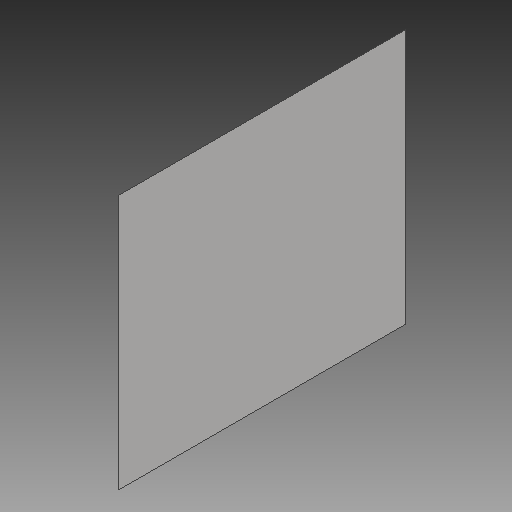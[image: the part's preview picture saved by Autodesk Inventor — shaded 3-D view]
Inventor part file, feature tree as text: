
AUTODESK INVENTOR PART (.ipt)
format: ipt  version: 2018 (Build 220112000, 112)  size: 78,336 bytes
history: native  units: mm
features: other x3, sketch x1
ambient origin geometry x8: Origin, YZ Plane, XZ Plane, XY Plane, X Axis, Y Axis, Z Axis, Center Point
bodies: Volumenkörper1 (feature_tree)
feature tree (4):
  other  "Wand2.ipt"
  other  "Volumenkörper1::Wand2.ipt"
  other  "Bezeichnung1"
  sketch  "Skizze1"  dims[d0=10.0mm]
